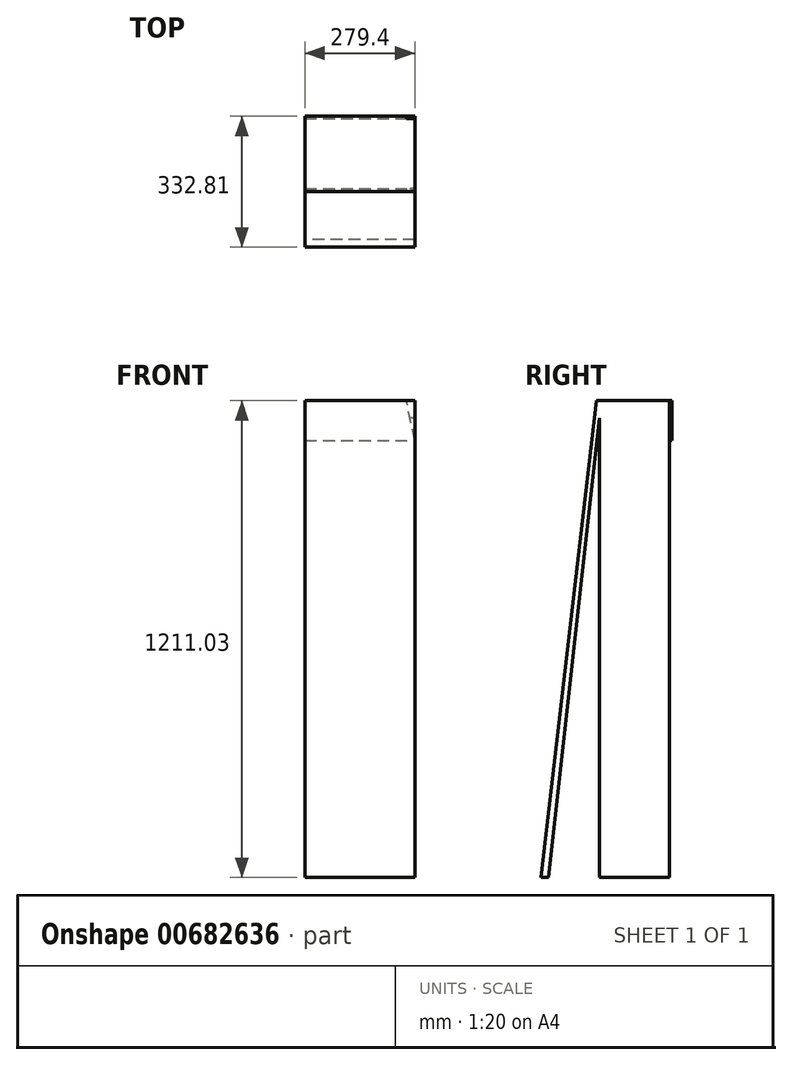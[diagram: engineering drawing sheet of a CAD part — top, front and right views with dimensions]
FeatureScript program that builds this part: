
annotation { "Feature Type Name" : "Feature", "Feature Type Description" : "" }
export const myFeature = defineFeature(function(context is Context, id is Id, definition is map)
    precondition{}
    {
        {
            var Q0;
            Q0=qCreatedBy(makeId("Top.planeOp"),FACE);
            var sketch = newSketch(context, id + "F0", { "sketchPlane" : qUnion([Q0])});
            skLineSegment(sketch, "E0.bottom", {"start": v(139.7, 95.25) * mm, "end": v(-139.7, 95.25) * mm});
            skLineSegment(sketch, "E0.top", {"start": v(139.7, -95.25) * mm, "end": v(-139.7, -95.25) * mm});
            skLineSegment(sketch, "E0.left", {"start": v(139.7, 95.25) * mm, "end": v(139.7, -95.25) * mm});
            skLineSegment(sketch, "E0.right", {"start": v(-139.7, 95.25) * mm, "end": v(-139.7, -95.25) * mm});
            skPoint(sketch, "E0.middle", {"position": v(0, 0) * mm});
            skSolve(sketch);
        }
        {
            var Q0;
            Q0=makeQuery(id+"F0.imprint","IMPRINT",FACE,{"disambiguationData":[TD([[makeQuery(id+"F0.imprint","IMPRINT",EDGE,{"derivedFrom":sQuery(id+"F0.wireOp",EDGE,"E0.bottom")}),1.0]])]});
            extrude(context, id + "F1", {"entities" : qUnion([Q0]), "oppositeDirection" : true, "depth" : 101.6 * mm, "offsetDistance" : 25 * mm});
        }
        {
            var Q0;
            Q0=makeQuery(id+"F1.opExtrude","SWEPT_FACE",FACE,{"disambiguationData":[OSD([sQuery(id+"F0.wireOp",EDGE,"E0.left")])]});
            var sketch = newSketch(context, id + "F2", { "sketchPlane" : qUnion([Q0])});
            skLineSegment(sketch, "E1.0.0", {"start": v(95.25, 0) * mm, "end": v(-95.25, 0) * mm});
            skLineSegment(sketch, "E1.0.1", {"start": v(-95.25, 0) * mm, "end": v(-95.25, -101.6) * mm});
            skLineSegment(sketch, "E1.0.2", {"start": v(-95.25, -101.6) * mm, "end": v(95.25, -101.6) * mm});
            skLineSegment(sketch, "E1.0.3", {"start": v(95.25, -101.6) * mm, "end": v(95.25, 0) * mm});
            skLineSegment(sketch, "E2", {"start": v(-95.25, -101.6) * mm, "end": v(-83.96, 0) * mm});
            skSolve(sketch);
        }
        {
            var Q0;
            {var subQ0=sQuery(id+"F2.wireOp",EDGE,"E1.0.1");Q0=makeQuery(id+"F2.imprint","IMPRINT",FACE,{"disambiguationData":[TD([[makeQuery(id+"F2.imprint","IMPRINT",EDGE,{"derivedFrom":subQ0}),-1.0]])]});}
            extrude(context, id + "F3", {"entities" : qUnion([Q0]), "operationType" : NewBodyOperationType.REMOVE, "endBound" : BoundingType.THROUGH_ALL, "oppositeDirection" : true, "depth" : 25 * mm, "offsetDistance" : 25 * mm});
        }
        {
            var Q0;
            Q0=makeQuery(id+"F1.opExtrude","SWEPT_FACE",FACE,{"disambiguationData":[OSD([sQuery(id+"F0.wireOp",EDGE,"E0.bottom")])]});
            var sketch = newSketch(context, id + "F4", { "sketchPlane" : qUnion([Q0])});
            skLineSegment(sketch, "E3.0.0", {"start": v(139.7, 0) * mm, "end": v(-139.7, 0) * mm});
            skLineSegment(sketch, "E3.0.1", {"start": v(-139.7, 0) * mm, "end": v(-139.7, -101.6) * mm});
            skLineSegment(sketch, "E3.0.2", {"start": v(-139.7, -101.6) * mm, "end": v(139.7, -101.6) * mm});
            skLineSegment(sketch, "E3.0.3", {"start": v(139.7, -101.6) * mm, "end": v(139.7, 0) * mm});
            skLineSegment(sketch, "E4", {"start": v(-139.7, -101.6) * mm, "end": v(-118.1, 0) * mm});
            skSolve(sketch);
        }
        {
            var Q0;
            {var subQ0=sQuery(id+"F4.wireOp",EDGE,"E3.0.1");Q0=makeQuery(id+"F4.imprint","IMPRINT",FACE,{"disambiguationData":[TD([[makeQuery(id+"F4.imprint","IMPRINT",EDGE,{"derivedFrom":subQ0}),-1.0]])]});}
            extrude(context, id + "F5", {"entities" : qUnion([Q0]), "operationType" : NewBodyOperationType.REMOVE, "endBound" : BoundingType.THROUGH_ALL, "oppositeDirection" : true, "depth" : 25 * mm, "offsetDistance" : 25 * mm});
        }
        {
            var Q0;
            Q0=qCreatedBy(makeId("Right.planeOp"),FACE);
            var sketch = newSketch(context, id + "F6", { "sketchPlane" : qUnion([Q0])});
            skLineSegment(sketch, "E5.0.0", {"start": v(95.25, -101.6) * mm, "end": v(83.96, 0) * mm});
            skLineSegment(sketch, "E5.0.1", {"start": v(83.96, 0) * mm, "end": v(-83.96, 0) * mm});
            skLineSegment(sketch, "E5.0.2", {"start": v(-83.96, 0) * mm, "end": v(-95.25, -101.6) * mm});
            skLineSegment(sketch, "E5.0.3", {"start": v(-95.25, -101.6) * mm, "end": v(95.25, -101.6) * mm});
            skLineSegment(sketch, "E6", {"start": v(-83.96, 0) * mm, "end": v(-96.69, 0) * mm});
            skLineSegment(sketch, "E7", {"start": v(-96.69, 0) * mm, "end": v(-237.56, -1211.03) * mm});
            skLineSegment(sketch, "E8", {"start": v(-237.56, -1211.03) * mm, "end": v(-218.5, -1211.03) * mm});
            skLineSegment(sketch, "E9", {"start": v(-218.5, -1211.03) * mm, "end": v(-95.25, -101.6) * mm});
            skSolve(sketch);
        }
        {
            var Q0;
            Q0=makeQuery(id+"F6.imprint","IMPRINT",FACE,{"disambiguationData":[TD([[makeQuery(id+"F6.imprint","IMPRINT",EDGE,{"derivedFrom":sQuery(id+"F6.wireOp",EDGE,"E5.0.2")}),-1.0]])]});
            extrude(context, id + "F7", {"entities" : qUnion([Q0]), "operationType" : NewBodyOperationType.ADD, "depth" : 139.7 * mm, "offsetDistance" : 25 * mm, "hasSecondDirection" : true, "secondDirectionOppositeDirection" : true, "secondDirectionDepth" : 139.7 * mm});
        }
        {
            var Q0;
            {var subQ0=sQuery(id+"F6.wireOp",EDGE,"E6");Q0=makeQuery(id+"FnlkDKlPEBF8tBP_1.1.F7.boolean.opBoolean","MERGE",FACE,{"derivedFrom":[makeQuery(id+"F7.boolean.opBoolean","MERGE",FACE,{"derivedFrom":[makeQuery(id+"F1.opExtrude","CAP_FACE",FACE,{"disambiguationData":[OSD([sQuery(id+"F0.wireOp",EDGE,"E0.bottom"),sQuery(id+"F0.wireOp",EDGE,"E0.top"),sQuery(id+"F0.wireOp",EDGE,"E0.left"),sQuery(id+"F0.wireOp",EDGE,"E0.right")])],"isStart":true}),makeQuery(id+"F7.opExtrude","SWEPT_FACE",FACE,{"disambiguationData":[OSD([subQ0])]})]}),makeQuery(id+"FnlkDKlPEBF8tBP_1.1.F7.opExtrude","SWEPT_FACE",FACE,{"disambiguationData":[OSD([subQ0])]})]});}
            var sketch = newSketch(context, id + "F8", { "sketchPlane" : qUnion([Q0])});
            skCircle(sketch, "E10", {"center": v(0, 0) * mm, "radius": 25.4 * mm});
            skSolve(sketch);
        }
        {
            var Q0;
            Q0=makeQuery(id+"F8.imprint","IMPRINT",FACE,{"disambiguationData":[TD([[makeQuery(id+"F8.imprint","IMPRINT",EDGE,{"derivedFrom":sQuery(id+"F8.wireOp",EDGE,"E10")}),1.0]])]});
            extrude(context, id + "F9", {"entities" : qUnion([Q0]), "operationType" : NewBodyOperationType.REMOVE, "endBound" : BoundingType.THROUGH_ALL, "oppositeDirection" : true, "depth" : 25 * mm, "offsetDistance" : 25 * mm});
        }
        {
            var Q0;
            Q0=qCreatedBy(makeId("Front.planeOp"),FACE);
            var sketch = newSketch(context, id + "F10", { "sketchPlane" : qUnion([Q0])});
            skLineSegment(sketch, "E11.0.0", {"start": v(-139.7, -101.6) * mm, "end": v(-118.1, 0) * mm});
            skLineSegment(sketch, "E11.0.1", {"start": v(-118.1, 0) * mm, "end": v(-139.7, 0) * mm});
            skLineSegment(sketch, "E11.0.2", {"start": v(-139.7, 0) * mm, "end": v(-139.7, -101.6) * mm});
            skLineSegment(sketch, "E12.0.0", {"start": v(-139.7, 0) * mm, "end": v(-139.7, -1211.03) * mm});
            skLineSegment(sketch, "E12.0.1", {"start": v(-139.7, -1211.03) * mm, "end": v(139.7, -1211.03) * mm});
            skLineSegment(sketch, "E12.0.2", {"start": v(139.7, -1211.03) * mm, "end": v(139.7, 0) * mm});
            skLineSegment(sketch, "E12.0.3", {"start": v(139.7, 0) * mm, "end": v(-139.7, 0) * mm});
            skLineSegment(sketch, "E13", {"start": v(-139.7, -1211.03) * mm, "end": v(-395, -1211.03) * mm});
            skLineSegment(sketch, "E14", {"start": v(-118.1, 0) * mm, "end": v(-375.52, -1211.03) * mm});
            skLineSegment(sketch, "E15", {"start": v(-375.52, -1211.03) * mm, "end": v(-395, -1211.03) * mm});
            skLineSegment(sketch, "E16", {"start": v(-395, -1211.03) * mm, "end": v(-137.58, 0) * mm});
            skPoint(sketch, "E17.orphan", {"position": v(-611.34, -1211.03) * mm});
            skSolve(sketch);
        }
        {
            var Q0;
            {var subQ0=sQuery(id+"F10.wireOp",EDGE,"E16");var subQ1=sQuery(id+"F10.wireOp",EDGE,"E12.0.0");var subQ2=makeQuery(id+"F10.imprint","INTERSECT",VERTEX,{"derivedFrom":[subQ1,subQ0]});Q0=makeQuery(id+"F10.imprint","IMPRINT",FACE,{"disambiguationData":[TD([[makeQuery(id+"F10.imprint","IMPRINT",EDGE,{"disambiguationData":[TD([[subQ2,-1.0]])],"derivedFrom":subQ1}),1.0]])]});}
            var Q1;
            {var subQ5=sQuery(id+"F10.wireOp",EDGE,"E15");Q1=makeQuery(id+"F10.imprint","IMPRINT",FACE,{"disambiguationData":[TD([[makeQuery(id+"F10.imprint","IMPRINT",EDGE,{"derivedFrom":subQ5}),-1.0]])]});}
            extrude(context, id + "F11", {"entities" : qUnion([Q0, Q1]), "operationType" : NewBodyOperationType.ADD, "depth" : 88.9 * mm, "offsetDistance" : 25 * mm, "hasSecondDirection" : true, "secondDirectionOppositeDirection" : true, "secondDirectionDepth" : 88.9 * mm});
        }
        {
            var Q0;
            {var subQ5=sQuery(id+"F10.wireOp",EDGE,"E15");Q0=makeQuery(id+"F10.imprint","IMPRINT",FACE,{"disambiguationData":[TD([[makeQuery(id+"F10.imprint","IMPRINT",EDGE,{"derivedFrom":subQ5}),-1.0]])]});}
            var Q1;
            {var subQ0=sQuery(id+"F10.wireOp",EDGE,"E16");var subQ1=sQuery(id+"F10.wireOp",EDGE,"E12.0.0");var subQ2=makeQuery(id+"F10.imprint","INTERSECT",VERTEX,{"derivedFrom":[subQ1,subQ0]});Q1=makeQuery(id+"F10.imprint","IMPRINT",FACE,{"disambiguationData":[TD([[makeQuery(id+"F10.imprint","IMPRINT",EDGE,{"disambiguationData":[TD([[subQ2,-1.0]])],"derivedFrom":subQ1}),1.0]])]});}
            extrude(context, id + "F12", {"entities" : qUnion([Q0, Q1]), "operationType" : NewBodyOperationType.ADD, "depth" : 25 * mm, "offsetDistance" : 25 * mm, "hasSecondDirection" : true, "secondDirectionOppositeDirection" : true, "secondDirectionDepth" : 25 * mm});
        }
    });
